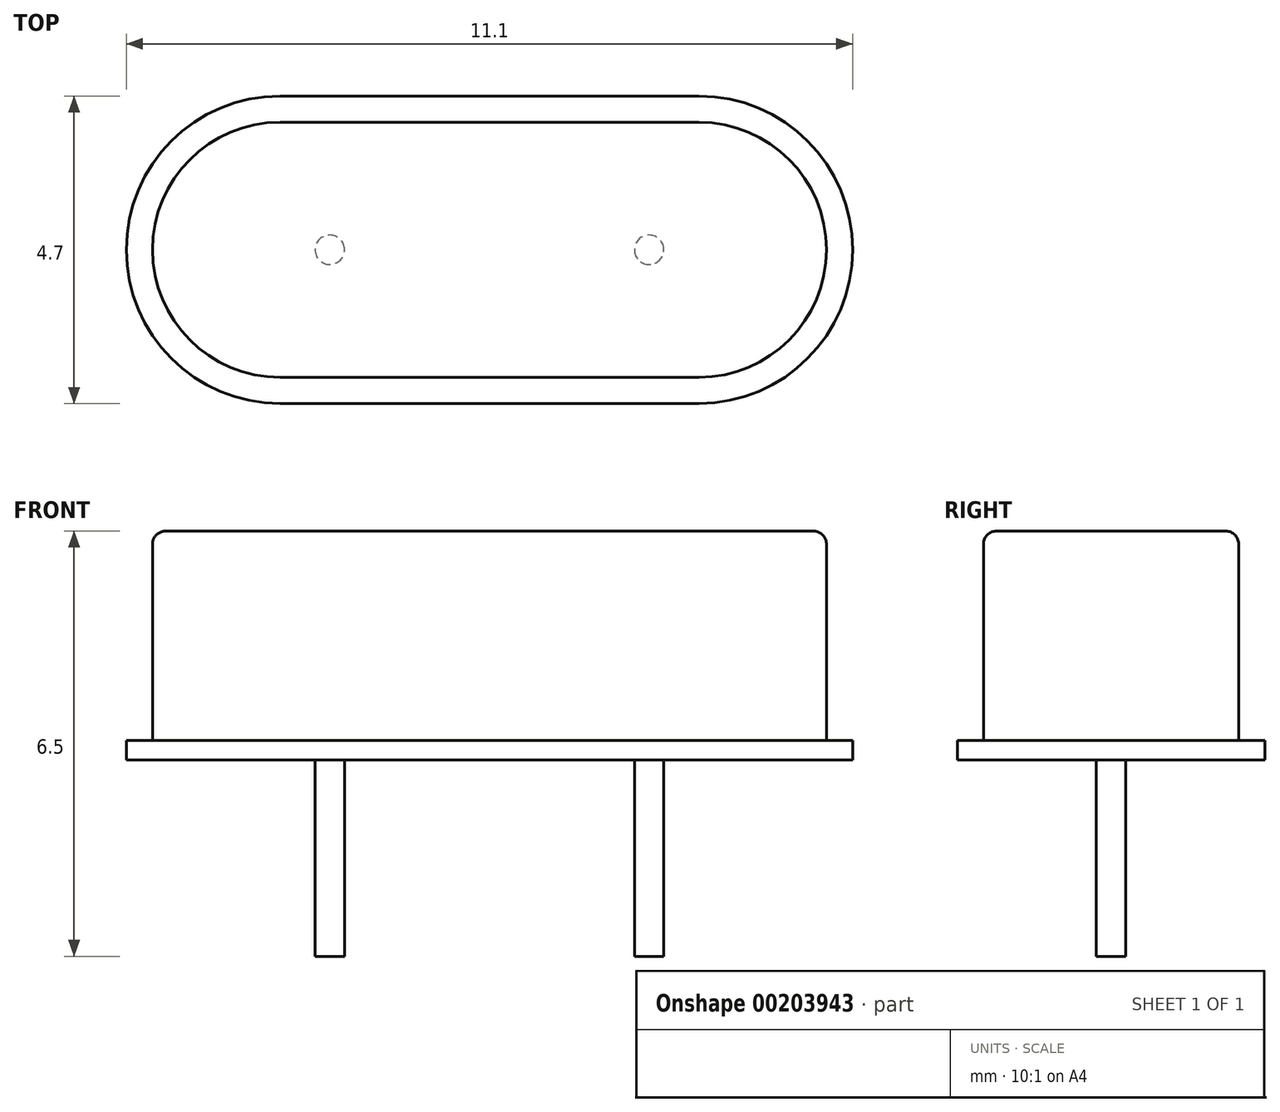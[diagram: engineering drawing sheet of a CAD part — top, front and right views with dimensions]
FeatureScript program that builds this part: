
annotation { "Feature Type Name" : "Feature", "Feature Type Description" : "" }
export const myFeature = defineFeature(function(context is Context, id is Id, definition is map)
    precondition{}
    {
        {
            var Q0;
            Q0=qCreatedBy(makeId("Top.planeOp"),FACE);
            var sketch = newSketch(context, id + "F0", { "sketchPlane" : qUnion([Q0])});
            skArc(sketch, "E0", {"start": v(-3.2, 2.35) * mm, "mid": v(-5.55, 0) * mm, "end": v(-3.2, -2.35) * mm});
            skArc(sketch, "E1", {"start": v(3.2, -2.35) * mm, "mid": v(5.55, 0) * mm, "end": v(3.2, 2.35) * mm});
            skLineSegment(sketch, "E2", {"start": v(-3.2, 2.35) * mm, "end": v(3.2, 2.35) * mm});
            skLineSegment(sketch, "E3", {"start": v(-3.2, -2.35) * mm, "end": v(3.2, -2.35) * mm});
            skSolve(sketch);
        }
        {
            var Q0;
            Q0=makeQuery(id+"F0.imprint","IMPRINT",FACE,{"disambiguationData":[TD([[makeQuery(id+"F0.imprint","IMPRINT",EDGE,{"derivedFrom":sQuery(id+"F0.wireOp",EDGE,"E0")}),1.0]])]});
            extrude(context, id + "F1", {"entities" : qUnion([Q0]), "depth" : 0.3 * mm});
        }
        {
            var Q0;
            Q0=makeQuery(id+"F1.opExtrude","CAP_FACE",FACE,{"disambiguationData":[OSD([sQuery(id+"F0.wireOp",EDGE,"E0"),sQuery(id+"F0.wireOp",EDGE,"E1"),sQuery(id+"F0.wireOp",EDGE,"E2"),sQuery(id+"F0.wireOp",EDGE,"E3")])],"isStart":false});
            var sketch = newSketch(context, id + "F2", { "sketchPlane" : qUnion([Q0])});
            skLineSegment(sketch, "E4.0", {"start": v(-3.2, 1.95) * mm, "end": v(3.2, 1.95) * mm});
            skArc(sketch, "E4.1", {"start": v(-3.2, 1.95) * mm, "mid": v(-5.15, 0) * mm, "end": v(-3.2, -1.95) * mm});
            skLineSegment(sketch, "E4.2", {"start": v(-3.2, -1.95) * mm, "end": v(3.2, -1.95) * mm});
            skArc(sketch, "E4.3", {"start": v(3.2, -1.95) * mm, "mid": v(5.15, 0) * mm, "end": v(3.2, 1.95) * mm});
            skSolve(sketch);
        }
        {
            var Q0;
            Q0=makeQuery(id+"F2.imprint","IMPRINT",FACE,{"disambiguationData":[TD([[makeQuery(id+"F2.imprint","IMPRINT",EDGE,{"derivedFrom":sQuery(id+"F2.wireOp",EDGE,"E4.0")}),-1.0]])]});
            extrude(context, id + "F3", {"entities" : qUnion([Q0]), "operationType" : NewBodyOperationType.ADD, "offsetDistance" : 25 * mm, "depth" : 3.2 * mm});
        }
        {
            var Q0;
            Q0=makeQuery(id+"F3.opExtrude","CAP_FACE",FACE,{"disambiguationData":[OSD([sQuery(id+"F2.wireOp",EDGE,"E4.0"),sQuery(id+"F2.wireOp",EDGE,"E4.1"),sQuery(id+"F2.wireOp",EDGE,"E4.2"),sQuery(id+"F2.wireOp",EDGE,"E4.3")])],"isStart":false});
            fillet(context, id + "F4", {"entities" : qUnion([Q0]), "radius" : 0.2 * mm, "tangentPropagation" : true, "allowEdgeOverflow" : false});
        }
        {
            var Q0;
            Q0=makeQuery(id+"F1.opExtrude","CAP_FACE",FACE,{"disambiguationData":[OSD([sQuery(id+"F0.wireOp",EDGE,"E0"),sQuery(id+"F0.wireOp",EDGE,"E1"),sQuery(id+"F0.wireOp",EDGE,"E2"),sQuery(id+"F0.wireOp",EDGE,"E3")])],"isStart":true});
            var sketch = newSketch(context, id + "F5", { "sketchPlane" : qUnion([Q0])});
            skLineSegment(sketch, "E5", {"start": v(-6.74, 0) * mm, "end": v(6.58, 0) * mm, "construction": true});
            skPoint(sketch, "E5.endSnap0", {"position": v(-5.55, 0) * mm});
            skLineSegment(sketch, "E6", {"start": v(0, 3.19) * mm, "end": v(0, -3.34) * mm, "construction": true});
            skCircle(sketch, "E7", {"center": v(-2.44, 0) * mm, "radius": 0.23 * mm});
            skCircle(sketch, "E8", {"center": v(2.44, 0) * mm, "radius": 0.23 * mm});
            skSolve(sketch);
        }
        {
            var Q0;
            Q0 = qSketchRegion(id + "F5", true);
            extrude(context, id + "F6", {"entities" : qUnion([Q0]), "operationType" : NewBodyOperationType.ADD, "offsetDistance" : 25 * mm, "depth" : 3 * mm});
        }
    });
